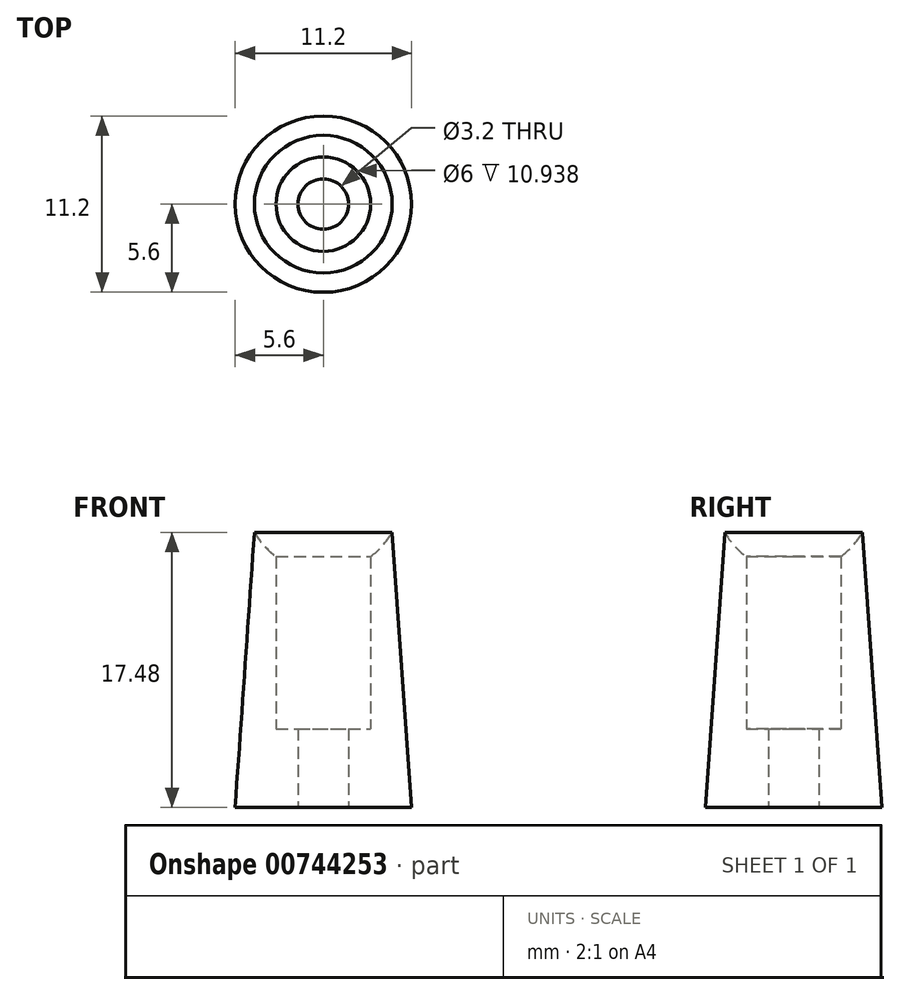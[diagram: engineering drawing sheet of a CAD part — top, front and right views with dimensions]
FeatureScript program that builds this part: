
annotation { "Feature Type Name" : "Feature", "Feature Type Description" : "" }
export const myFeature = defineFeature(function(context is Context, id is Id, definition is map)
    precondition{}
    {
        {
            var Q0;
            Q0=qCreatedBy(makeId("Front.planeOp"),FACE);
            var sketch = newSketch(context, id + "F0", { "sketchPlane" : qUnion([Q0])});
            skLineSegment(sketch, "E0", {"start": v(0, 0) * mm, "end": v(1.6, 0) * mm});
            skLineSegment(sketch, "E1", {"start": v(1.6, 0) * mm, "end": v(5.6, 0) * mm});
            skLineSegment(sketch, "E2", {"start": v(0, 0) * mm, "end": v(0, 20) * mm});
            skCircle(sketch, "E3", {"center": v(0, 20) * mm, "radius": 5.05 * mm});
            skLineSegment(sketch, "E4", {"start": v(0, 20) * mm, "end": v(5.05, 20) * mm});
            skLineSegment(sketch, "E5", {"start": v(0, 20) * mm, "end": v(4.37, 17.48) * mm});
            skLineSegment(sketch, "E6", {"start": v(4.37, 17.48) * mm, "end": v(5.6, 0) * mm});
            skLineSegment(sketch, "E7", {"start": v(1.6, 0) * mm, "end": v(1.6, 15.21) * mm});
            skLineSegment(sketch, "E8", {"start": v(0, 0) * mm, "end": v(0, 5) * mm});
            skLineSegment(sketch, "E9", {"start": v(0, 5) * mm, "end": v(3, 5) * mm});
            skLineSegment(sketch, "E10", {"start": v(3, 5) * mm, "end": v(3, 15.94) * mm});
            skSolve(sketch);
        }
        {
            var Q0;
            {var subQ1=sQuery(id+"F0.wireOp",EDGE,"E1");Q0=makeQuery(id+"F0.imprint","IMPRINT",FACE,{"disambiguationData":[TD([[makeQuery(id+"F0.imprint","IMPRINT",EDGE,{"derivedFrom":subQ1}),1.0]])]});}
            var Q1;
            Q1=sQuery(id+"F0.wireOp",EDGE,"E2");
            revolve(context, id + "F1", {"surfaceOperationType" : NewSurfaceOperationType.NEW, "entities" : qUnion([Q0]), "axis" : qUnion([Q1]), "revolveType" : RevolveType.FULL});
        }
    });
